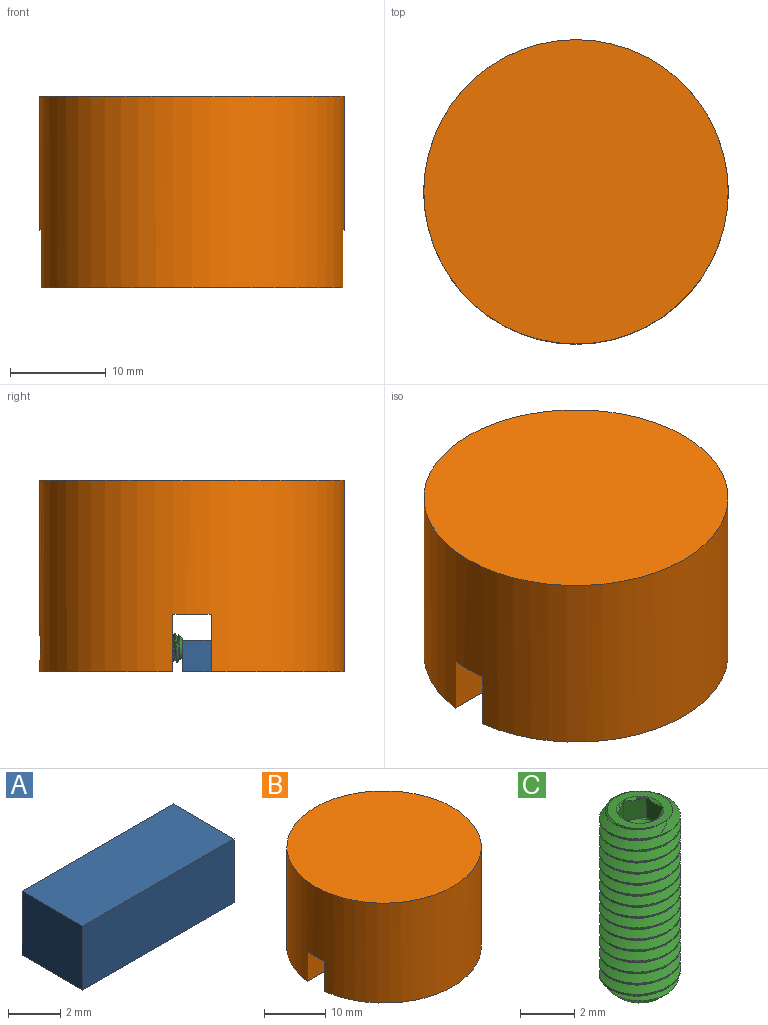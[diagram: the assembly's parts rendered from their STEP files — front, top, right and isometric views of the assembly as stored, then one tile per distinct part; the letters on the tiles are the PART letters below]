
ASSEMBLY  parts=3 mates=4
PART A: 6 faces, bbox 8.2x3.3x3 mm
  f0: plane 3.3x3mm, normal (1,0,0), area 9.9mm2, adj f1,f3,f4,f5
  f1: plane 8.2x3mm, normal (0,1,0), area 24.6mm2, adj f0,f2,f4,f5
  f2: plane 3.3x3mm, normal (-1,0,0), area 9.9mm2, adj f1,f3,f4,f5
  f3: plane 8.2x3mm, normal (0,-1,0), area 24.6mm2, adj f0,f2,f4,f5
  f4: plane 8.2x3.3mm, normal (0,0,1), area 27.1mm2, adj f0,f1,f2,f3
  f5: plane 8.2x3.3mm, normal (0,0,-1), area 27.1mm2, adj f0,f1,f2,f3
PART B: 10 faces, bbox 31.8x31.8x20 mm
  f0: cylinder r=15.88mm len=31.75mm, axis (0,0,-1), area 1939.7mm2, adj f1,f2,f3,f4,f5,f6,f8
  f1: plane 31.5x13.88mm, normal (0,0,-1), area 332.5mm2, adj f0,f5
  f2: plane 31.75x31.75mm, normal (0,0,1), area 791.7mm2, adj f0
  f3: plane 31.5x13.88mm, normal (0,0,-1), area 332.5mm2, adj f0,f6
  f4: plane 31.75x4mm, normal (0,0,-1), area 126.7mm2, adj f0,f5,f6
  f5: plane 31.5x6mm, normal (0,-1,0), area 183.3mm2, adj f0,f1,f4,f7
  f6: plane 31.5x6mm, normal (0,1,0), area 189mm2, adj f0,f3,f4
  f7: cylinder r=1.35mm len=6.88mm, axis (0,-1,0), area 58.3mm2, adj f5,f9
  f8: cylinder r=1.5mm len=7mm, axis (0,1,0), area 65.6mm2, adj f0,f9
  f9: plane 3x3mm, normal (0,1,0), area 1.3mm2, adj f7,f8
PART C: 28 faces, bbox 3.7x3.3x8.6 mm
  f0: plane 0.65x0.38mm, normal (0,0,1), area 0mm2, adj f1,f26,f27
  f1: plane 1.22x1.03mm, normal (0.5,-0.87,0), area 0.8mm2, adj f0,f2,f3,f25,f27
  f2: plane 0.75x0.22mm, normal (0,0,1), area 0mm2, adj f1,f25,f26
  f3: cone r=0.87mm half-angle=55deg, axis (0,0,1), area 0mm2, adj f1,f4
  f4: plane 2.4x2.39mm, normal (0,0,1), area 2.1mm2, adj f3,f5,f10,f11,f12,f13,f14,f22
  f5: bspline ~8.1x3.46mm, area 47.8mm2, adj f4,f6,f9,f10,f12
  f6: cone r=1mm half-angle=45deg, axis (0,0,1), area 0.5mm2, adj f5,f7,f9,f11
  f7: cone r=1mm half-angle=45deg, axis (0,0,1), area 3.1mm2, adj f6,f8,f11,f12
  f8: plane 2x2mm, normal (0,0,-1), area 3.1mm2, adj f7
  f9: cylinder r=1.5mm len=7.29mm, axis (0,0,-1), area 5.1mm2, adj f5,f6,f10,f11
  f10: cone r=1.5mm half-angle=55deg, axis (0,0,-1), area 1.4mm2, adj f4,f5,f9,f11
  f11: bspline ~8.1x3.46mm, area 47.8mm2, adj f4,f6,f7,f9,f10,f12
  f12: cylinder r=1.18mm len=7.82mm, axis (0,0,-1), area 13.4mm2, adj f4,f5,f7,f11
  f13: cone r=0.87mm half-angle=55deg, axis (0,0,1), area 0mm2, adj f4,f27
  f14: cone r=0.87mm half-angle=55deg, axis (0,0,1), area 0mm2, adj f4,f15
  f15: plane 1.22x1.03mm, normal (0.5,0.87,0), area 0.8mm2, adj f14,f16,f17,f18,f27
  f16: plane 0.65x0.38mm, normal (0,0,1), area 0mm2, adj f15,f26,f27
  f17: plane 0.75x0.22mm, normal (0,0,1), area 0mm2, adj f15,f18,f26
  f18: plane 1.22x1.03mm, normal (-0.5,0.87,0), area 0.8mm2, adj f15,f17,f19,f20,f22
  f19: plane 0.65x0.38mm, normal (0,0,1), area 0mm2, adj f18,f20,f26
  f20: plane 1.22x1.15mm, normal (-1,0,0), area 0.8mm2, adj f18,f19,f21,f23,f25
  f21: plane 0.65x0.38mm, normal (0,0,1), area 0mm2, adj f20,f25,f26
  f22: cone r=0.87mm half-angle=55deg, axis (0,0,1), area 0mm2, adj f4,f18
  f23: cone r=0.87mm half-angle=55deg, axis (0,0,1), area 0mm2, adj f4,f20
  f24: cone r=0.87mm half-angle=55deg, axis (0,0,1), area 0mm2, adj f4,f25
  f25: plane 1.22x1.03mm, normal (-0.5,-0.87,0), area 0.8mm2, adj f1,f2,f20,f21,f24
  f26: cone r=0.75mm half-angle=60deg, axis (0,0,1), area 2mm2, adj f0,f2,f16,f17,f19,f21
  f27: plane 1.22x1.15mm, normal (1,0,0), area 0.8mm2, adj f0,f1,f13,f15,f16
PLACE A rot(axis=(-1,0,0),90deg) t=(3.62,40.42,2.36)mm
PLACE B rot(axis=(0,0.16,0.99),0deg) t=(3.59,42.42,0.71)mm
PLACE C rot(axis=(-1,0,0),90deg) t=(3.59,47.42,3.21)mm
MATE planar A.f1 <-> B.f3  axis (0,0,-1) through (3.62,41.92,0.71)mm
MATE planar A.f5 <-> B.f6  axis (0,1,0) through (-0.48,40.42,0.71)mm
MATE cylindrical C.f6 <-> B.f7  axis (0,-1,0) through (3.59,43.42,3.21)mm
MATE planar C.f6 <-> A.f4  axis (0,-1,0) through (3.59,43.42,3.21)mm
